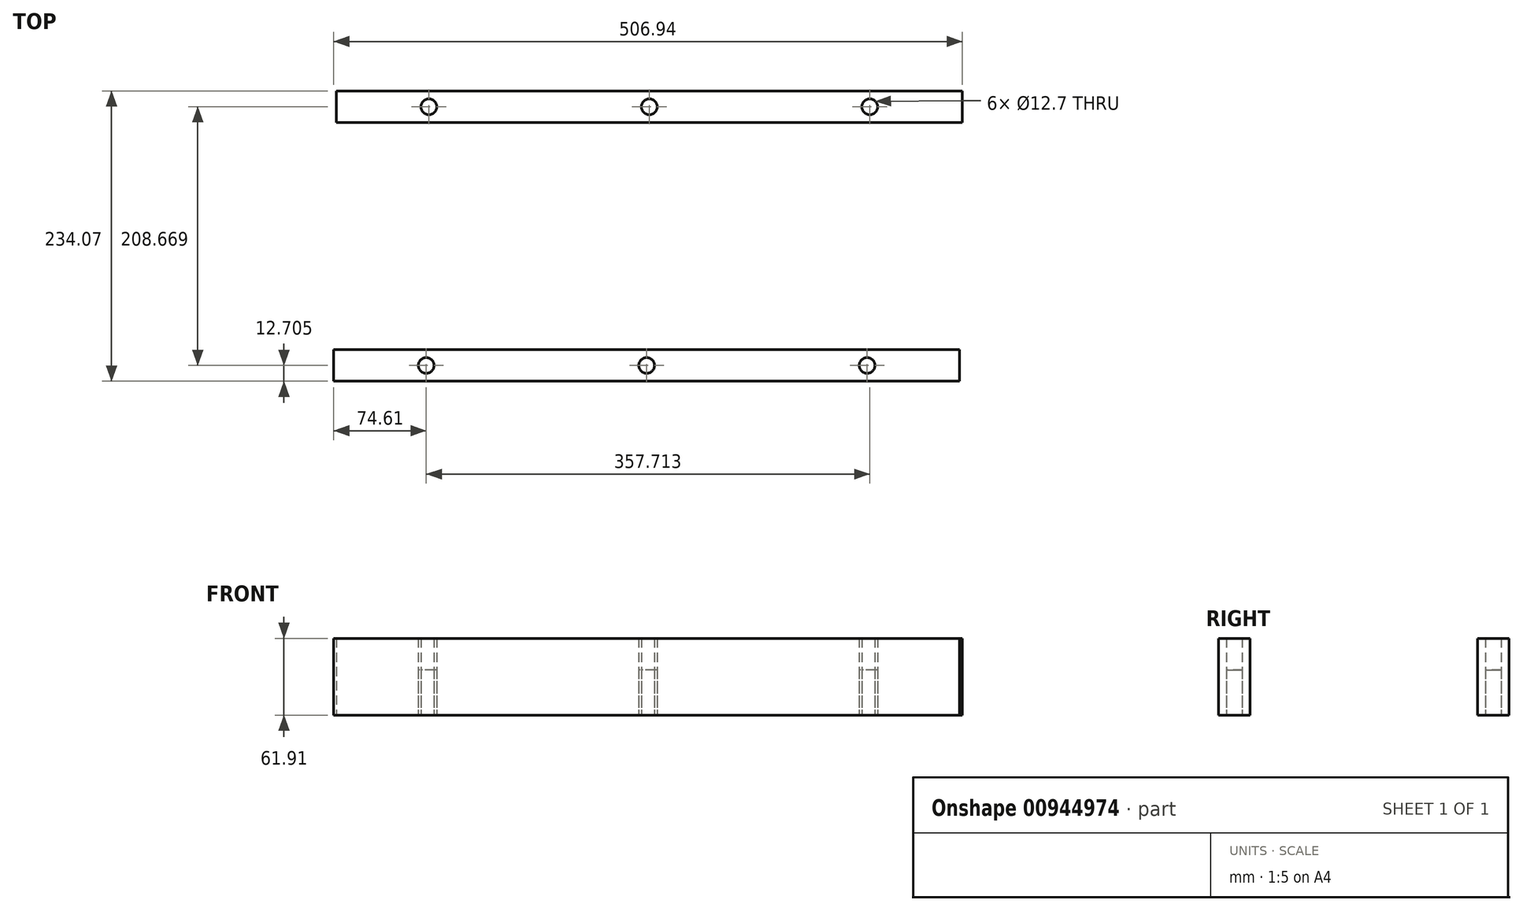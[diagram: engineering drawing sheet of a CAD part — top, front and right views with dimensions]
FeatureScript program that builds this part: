
annotation { "Feature Type Name" : "Feature", "Feature Type Description" : "" }
export const myFeature = defineFeature(function(context is Context, id is Id, definition is map)
    precondition{}
    {
        {
            var Q0;
            Q0=qCreatedBy(makeId("Top.planeOp"),FACE);
            var sketch = newSketch(context, id + "F0", { "sketchPlane" : qUnion([Q0])});
            skLineSegment(sketch, "E0.bottom", {"start": v(-270.34, 60.15) * mm, "end": v(234.49, 60.15) * mm});
            skLineSegment(sketch, "E0.top", {"start": v(-270.34, 34.75) * mm, "end": v(234.49, 34.75) * mm});
            skLineSegment(sketch, "E0.left", {"start": v(-270.34, 60.15) * mm, "end": v(-270.34, 34.75) * mm});
            skLineSegment(sketch, "E0.right", {"start": v(234.49, 60.15) * mm, "end": v(234.49, 34.75) * mm});
            skCircle(sketch, "E1", {"center": v(-195.73, 47.45) * mm, "radius": 6.35 * mm});
            skCircle(sketch, "E2", {"center": v(-17.93, 47.45) * mm, "radius": 6.35 * mm});
            skCircle(sketch, "E3", {"center": v(159.87, 47.45) * mm, "radius": 6.35 * mm});
            skLineSegment(sketch, "E4.bottom", {"start": v(-272.45, -148.52) * mm, "end": v(232.37, -148.52) * mm});
            skLineSegment(sketch, "E4.top", {"start": v(-272.45, -173.92) * mm, "end": v(232.37, -173.92) * mm});
            skLineSegment(sketch, "E4.left", {"start": v(-272.45, -148.52) * mm, "end": v(-272.45, -173.92) * mm});
            skLineSegment(sketch, "E4.right", {"start": v(232.37, -148.52) * mm, "end": v(232.37, -173.92) * mm});
            skCircle(sketch, "E5", {"center": v(-197.84, -161.22) * mm, "radius": 6.35 * mm});
            skCircle(sketch, "E6", {"center": v(-20.04, -161.22) * mm, "radius": 6.35 * mm});
            skCircle(sketch, "E7", {"center": v(157.76, -161.22) * mm, "radius": 6.35 * mm});
            skSolve(sketch);
        }
        {
            var Q0;
            Q0=makeQuery(id+"F0.imprint","IMPRINT",FACE,{"disambiguationData":[TD([[makeQuery(id+"F0.imprint","IMPRINT",EDGE,{"derivedFrom":sQuery(id+"F0.wireOp",EDGE,"E0.bottom")}),-1.0]])]});
            var Q1;
            Q1=makeQuery(id+"F0.imprint","IMPRINT",FACE,{"disambiguationData":[TD([[makeQuery(id+"F0.imprint","IMPRINT",EDGE,{"derivedFrom":sQuery(id+"F0.wireOp",EDGE,"E4.bottom")}),-1.0]])]});
            extrude(context, id + "F1", {"entities" : qUnion([Q0, Q1]), "depth" : 61.9 * mm, "offsetDistance" : 25.4 * mm});
        }
        {
            var Q0;
            Q0=makeQuery(id+"F0.imprint","IMPRINT",FACE,{"disambiguationData":[TD([[makeQuery(id+"F0.imprint","IMPRINT",EDGE,{"derivedFrom":sQuery(id+"F0.wireOp",EDGE,"E1")}),1.0]])]});
            var Q1;
            Q1=makeQuery(id+"F0.imprint","IMPRINT",FACE,{"disambiguationData":[TD([[makeQuery(id+"F0.imprint","IMPRINT",EDGE,{"derivedFrom":sQuery(id+"F0.wireOp",EDGE,"E2")}),1.0]])]});
            var Q2;
            Q2=makeQuery(id+"F0.imprint","IMPRINT",FACE,{"disambiguationData":[TD([[makeQuery(id+"F0.imprint","IMPRINT",EDGE,{"derivedFrom":sQuery(id+"F0.wireOp",EDGE,"E3")}),1.0]])]});
            var Q3;
            Q3=makeQuery(id+"F0.imprint","IMPRINT",FACE,{"disambiguationData":[TD([[makeQuery(id+"F0.imprint","IMPRINT",EDGE,{"derivedFrom":sQuery(id+"F0.wireOp",EDGE,"E5")}),1.0]])]});
            var Q4;
            Q4=makeQuery(id+"F0.imprint","IMPRINT",FACE,{"disambiguationData":[TD([[makeQuery(id+"F0.imprint","IMPRINT",EDGE,{"derivedFrom":sQuery(id+"F0.wireOp",EDGE,"E6")}),1.0]])]});
            var Q5;
            Q5=makeQuery(id+"F0.imprint","IMPRINT",FACE,{"disambiguationData":[TD([[makeQuery(id+"F0.imprint","IMPRINT",EDGE,{"derivedFrom":sQuery(id+"F0.wireOp",EDGE,"E7")}),1.0]])]});
            extrude(context, id + "F2", {"entities" : qUnion([Q0, Q1, Q2, Q3, Q4, Q5]), "depth" : 36.5 * mm, "offsetDistance" : 25.4 * mm});
        }
    });
